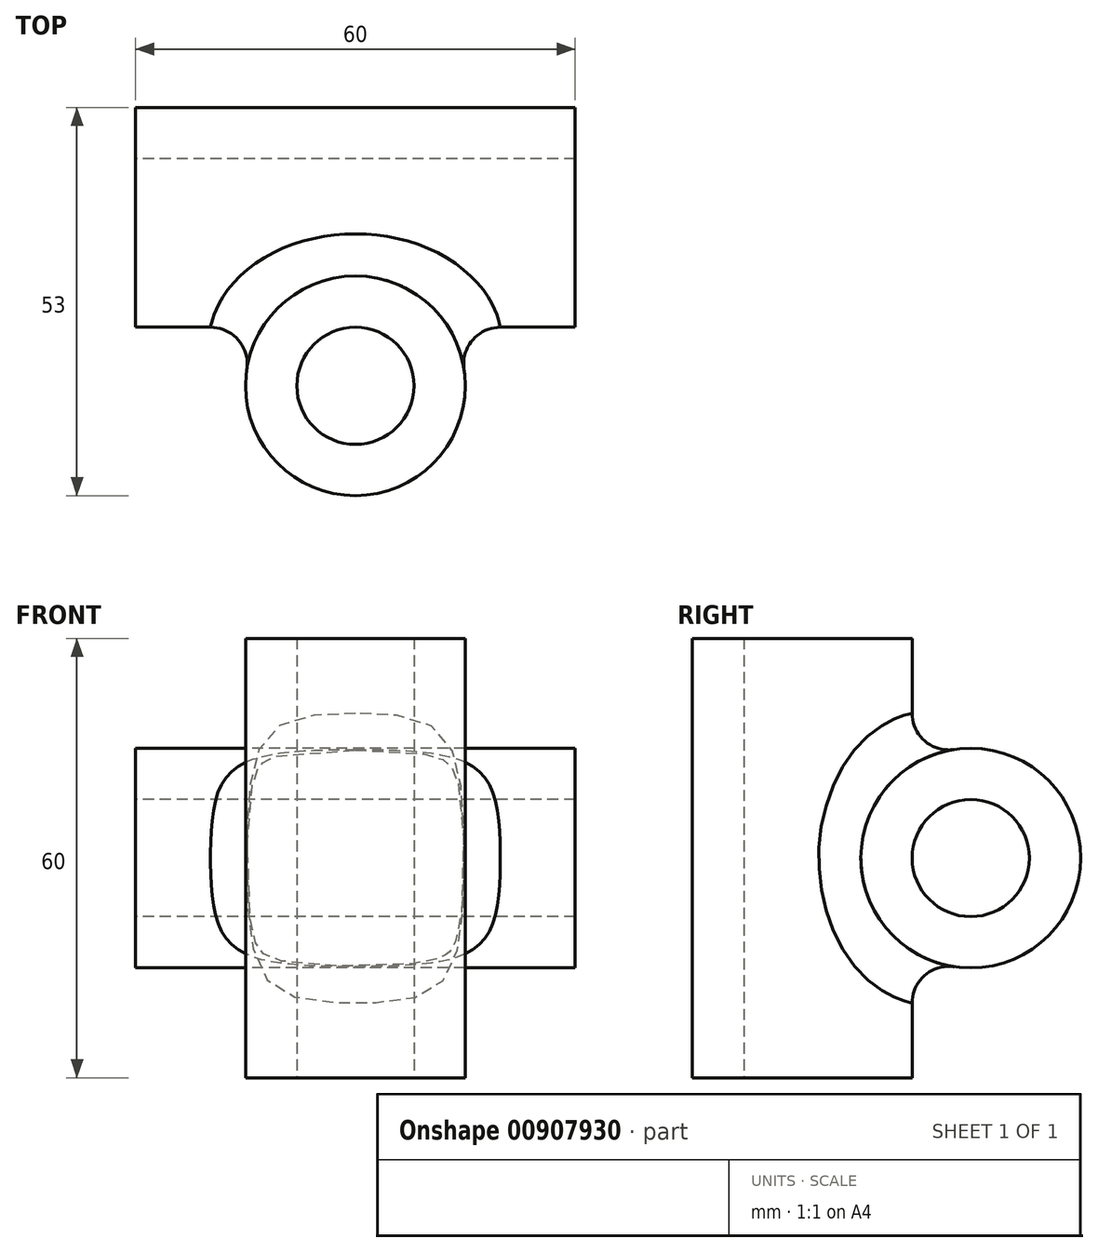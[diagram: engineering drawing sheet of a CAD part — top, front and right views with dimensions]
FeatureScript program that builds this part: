
annotation { "Feature Type Name" : "Feature", "Feature Type Description" : "" }
export const myFeature = defineFeature(function(context is Context, id is Id, definition is map)
    precondition{}
    {
        {
            var Q0;
            Q0=qCreatedBy(makeId("Top.planeOp"),FACE);
            var sketch = newSketch(context, id + "F0", { "sketchPlane" : qUnion([Q0])});
            skCircle(sketch, "E0", {"center": v(0, 0) * mm, "radius": 15 * mm});
            skCircle(sketch, "E1", {"center": v(0, 0) * mm, "radius": 8 * mm});
            skSolve(sketch);
        }
        {
            var Q0;
            Q0 = qSketchRegion(id + "F0", true);
            extrude(context, id + "F1", {"entities" : qUnion([Q0]), "endBound" : BoundingType.SYMMETRIC, "depth" : 60 * mm, "offsetDistance" : 25 * mm});
        }
        {
            var Q0;
            Q0=qCreatedBy(makeId("Right.planeOp"),FACE);
            var sketch = newSketch(context, id + "F2", { "sketchPlane" : qUnion([Q0])});
            skCircle(sketch, "E2", {"center": v(23, 0) * mm, "radius": 15 * mm});
            skCircle(sketch, "E3", {"center": v(23, 0) * mm, "radius": 8 * mm});
            skSolve(sketch);
        }
        {
            var Q0;
            Q0 = qSketchRegion(id + "F2", true);
            extrude(context, id + "F3", {"entities" : qUnion([Q0]), "operationType" : NewBodyOperationType.ADD, "endBound" : BoundingType.SYMMETRIC, "depth" : 60 * mm, "offsetDistance" : 25 * mm});
        }
        {
            var Q0;
            Q0=makeQuery(id+"F3.boolean.opBoolean","INTERSECT",EDGE,{"derivedFrom":[makeQuery(id+"F1.opExtrude","SWEPT_FACE",FACE,{"disambiguationData":[OSD([sQuery(id+"F0.wireOp",EDGE,"E0")])]}),makeQuery(id+"F3.opExtrude","SWEPT_FACE",FACE,{"disambiguationData":[OSD([sQuery(id+"F2.wireOp",EDGE,"E2")])]})]});
            fillet(context, id + "F4", {"entities" : qUnion([Q0]), "radius" : 5 * mm, "tangentPropagation" : true, "allowEdgeOverflow" : false});
        }
    });
